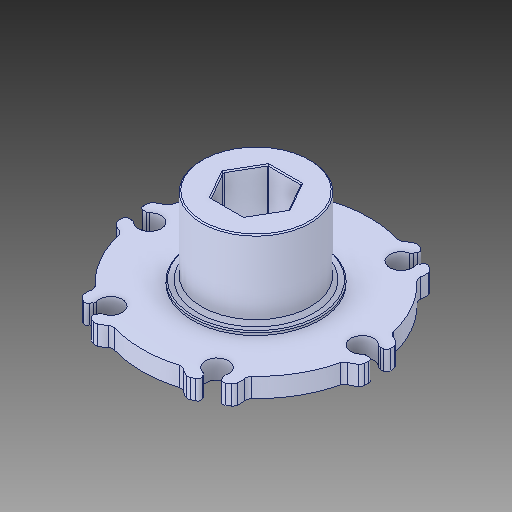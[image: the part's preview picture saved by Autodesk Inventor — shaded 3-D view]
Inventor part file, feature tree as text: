
AUTODESK INVENTOR PART (.ipt)
format: ipt  version: 2018 (Build 220112000, 112)  size: 286,208 bytes
history: native  units: in
note: dims shown in document units (in); Inventor stores cm internally (conversion verified against a paired STEP export)
features: fillet x1
ambient origin geometry x8: Origin, YZ Plane, XZ Plane, XY Plane, X Axis, Y Axis, Z Axis, Center Point
bodies: Solid1 (feature_tree)
feature tree (1):
  fillet  "Fillet7"  [1 undecoded]
note: 1 required parameter value undecoded (feature->parameter linkage not recoverable at this tier; creation-order binding heuristic only, values carry confidence <= 0.55)
